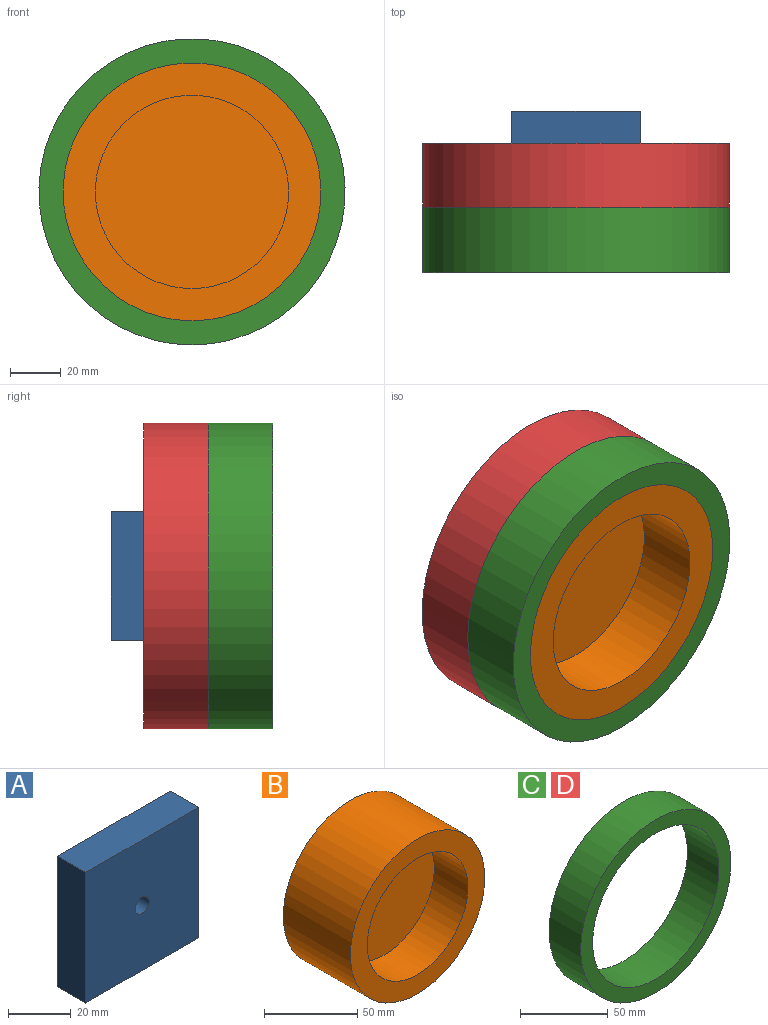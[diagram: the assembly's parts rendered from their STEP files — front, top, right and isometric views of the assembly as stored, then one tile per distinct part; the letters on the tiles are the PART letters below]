
ASSEMBLY  parts=4 mates=3
PART A: 7 faces, bbox 50.8x12.7x50.8 mm
  f0: plane 50.8x12.7mm, normal (1,0,0), area 645.2mm2, adj f1,f3,f4,f5
  f1: plane 50.8x12.7mm, normal (0,0,1), area 645.2mm2, adj f0,f2,f4,f5
  f2: plane 50.8x12.7mm, normal (-1,0,0), area 645.2mm2, adj f1,f3,f4,f5
  f3: plane 50.8x12.7mm, normal (0,0,-1), area 645.2mm2, adj f0,f2,f4,f5
  f4: plane 50.8x50.8mm, normal (0,-1,0), area 2549mm2, adj f0,f1,f2,f3,f6
  f5: plane 50.8x50.8mm, normal (0,1,0), area 2549mm2, adj f0,f1,f2,f3,f6
  f6: cylinder r=3.17mm len=12.7mm, axis (0,-1,0), area 253.4mm2, adj f4,f5
PART B: 5 faces, bbox 101.6x50.8x101.6 mm
  f0: cylinder r=50.8mm len=101.6mm, axis (0,1,0), area 16214.6mm2, adj f1,f2
  f1: plane 101.6x101.6mm, normal (0,-1,0), area 3547mm2, adj f0,f3
  f2: plane 101.6x101.6mm, normal (0,1,0), area 8107.3mm2, adj f0
  f3: cylinder r=38.1mm len=76.2mm, axis (0,-1,0), area 6080.5mm2, adj f1,f4
  f4: plane 76.2x76.2mm, normal (0,-1,0), area 4560.4mm2, adj f3
PART C: 4 faces, bbox 120.7x25.4x120.7 mm
  f0: cylinder r=50.8mm len=101.6mm, axis (0,1,0), area 8107.3mm2, adj f2,f3
  f1: cylinder r=60.32mm len=120.65mm, axis (0,1,0), area 9627.4mm2, adj f2,f3
  f2: plane 120.65x120.65mm, normal (0,-1,0), area 3325.3mm2, adj f0,f1
  f3: plane 120.65x120.65mm, normal (0,1,0), area 3325.3mm2, adj f0,f1
PART D: same geometry as C
PLACE A t=(0,12.7,0)mm
PLACE B at identity
PLACE C t=(0,-25.4,0)mm
PLACE D at identity
MATE fastened B.f0 <-> A.f6  axis (0,1,0) through (0,0,0)mm
MATE fastened C.f0 <-> B.f3  axis (0,-1,0) through (0,-50.8,0)mm
MATE fastened D.f0 <-> B.f0  axis (0,1,0) through (0,0,0)mm
